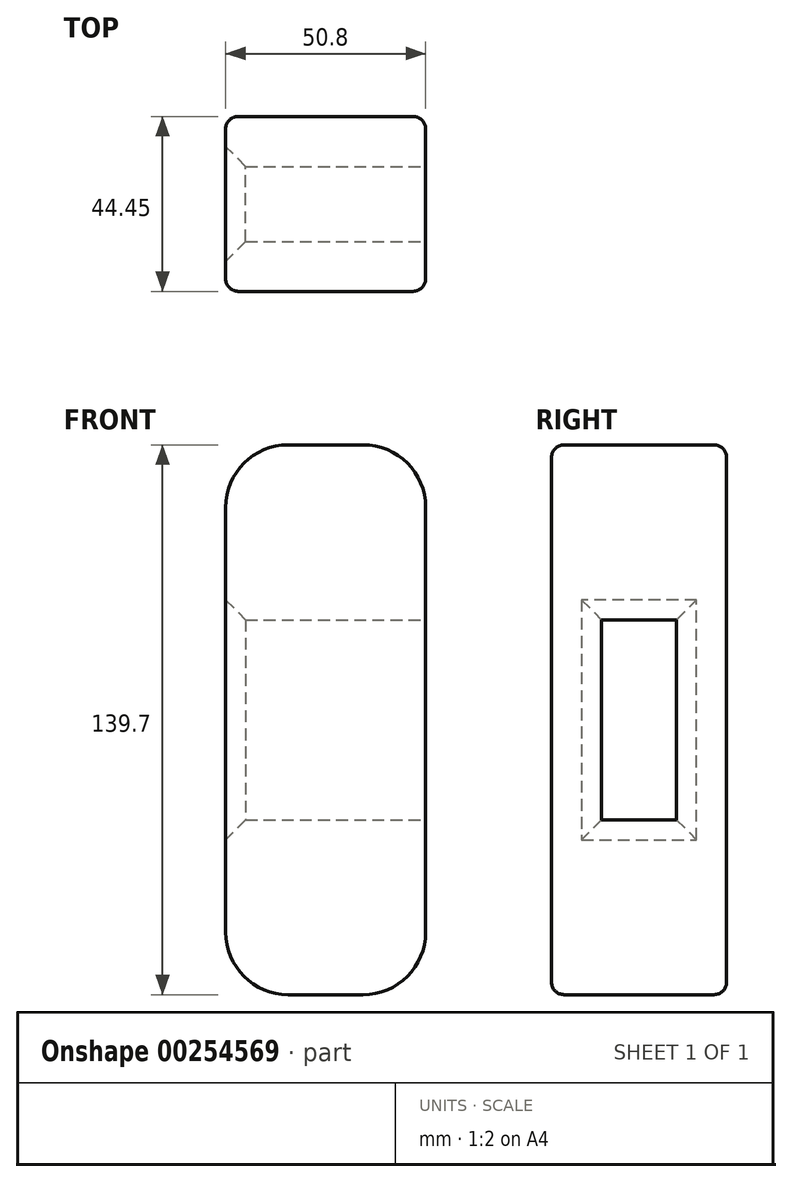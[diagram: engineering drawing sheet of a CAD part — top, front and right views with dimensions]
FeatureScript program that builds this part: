
annotation { "Feature Type Name" : "Feature", "Feature Type Description" : "" }
export const myFeature = defineFeature(function(context is Context, id is Id, definition is map)
    precondition{}
    {
        {
            var Q0;
            Q0=qCreatedBy(makeId("Front.planeOp"),FACE);
            var sketch = newSketch(context, id + "F0", { "sketchPlane" : qUnion([Q0])});
            skLineSegment(sketch, "E0.bottom", {"start": v(9.52, 69.85) * mm, "end": v(-9.53, 69.85) * mm});
            skLineSegment(sketch, "E0.top", {"start": v(9.52, -69.85) * mm, "end": v(-9.53, -69.85) * mm});
            skLineSegment(sketch, "E0.left", {"start": v(25.4, 53.98) * mm, "end": v(25.4, -53.97) * mm});
            skLineSegment(sketch, "E0.right", {"start": v(-25.4, 53.98) * mm, "end": v(-25.4, -53.97) * mm});
            skPoint(sketch, "E0.middle", {"position": v(0, 0) * mm});
            skPoint(sketch, "E1.visualSharp", {"position": v(-25.4, 69.85) * mm});
            skArc(sketch, "E1.filletArc", {"start": v(-9.53, 69.85) * mm, "mid": v(-20.75, 65.2) * mm, "end": v(-25.4, 53.98) * mm});
            skPoint(sketch, "E2.visualSharp", {"position": v(25.4, 69.85) * mm});
            skArc(sketch, "E2.filletArc", {"start": v(25.4, 53.98) * mm, "mid": v(20.75, 65.2) * mm, "end": v(9.52, 69.85) * mm});
            skPoint(sketch, "E3.visualSharp", {"position": v(25.4, -69.85) * mm});
            skArc(sketch, "E3.filletArc", {"start": v(9.52, -69.85) * mm, "mid": v(20.75, -65.2) * mm, "end": v(25.4, -53.97) * mm});
            skPoint(sketch, "E4.visualSharp", {"position": v(-25.4, -69.85) * mm});
            skArc(sketch, "E4.filletArc", {"start": v(-25.4, -53.97) * mm, "mid": v(-20.75, -65.2) * mm, "end": v(-9.53, -69.85) * mm});
            skSolve(sketch);
        }
        {
            var Q0;
            Q0 = qSketchRegion(id + "F0", true);
            extrude(context, id + "F1", {"entities" : qUnion([Q0]), "depth" : 44.45 * mm});
        }
        {
            var Q0;
            Q0=makeQuery(id+"F1.opExtrude","CAP_FACE",FACE,{"disambiguationData":[OSD([sQuery(id+"F0.wireOp",EDGE,"E0.bottom"),sQuery(id+"F0.wireOp",EDGE,"E0.top"),sQuery(id+"F0.wireOp",EDGE,"E0.left"),sQuery(id+"F0.wireOp",EDGE,"E0.right"),sQuery(id+"F0.wireOp",EDGE,"E1.filletArc"),sQuery(id+"F0.wireOp",EDGE,"E2.filletArc"),sQuery(id+"F0.wireOp",EDGE,"E3.filletArc"),sQuery(id+"F0.wireOp",EDGE,"E4.filletArc")])],"isStart":false});
            var Q1;
            Q1=makeQuery(id+"F1.opExtrude","CAP_FACE",FACE,{"disambiguationData":[OSD([sQuery(id+"F0.wireOp",EDGE,"E0.bottom"),sQuery(id+"F0.wireOp",EDGE,"E0.top"),sQuery(id+"F0.wireOp",EDGE,"E0.left"),sQuery(id+"F0.wireOp",EDGE,"E0.right"),sQuery(id+"F0.wireOp",EDGE,"E1.filletArc"),sQuery(id+"F0.wireOp",EDGE,"E2.filletArc"),sQuery(id+"F0.wireOp",EDGE,"E3.filletArc"),sQuery(id+"F0.wireOp",EDGE,"E4.filletArc")])],"isStart":true});
            fillet(context, id + "F2", {"entities" : qUnion([Q0, Q1]), "radius" : 3.17 * mm, "tangentPropagation" : true, "allowEdgeOverflow" : false});
        }
        {
            var Q0;
            Q0=makeQuery(id+"F1.opExtrude","SWEPT_FACE",FACE,{"disambiguationData":[OSD([sQuery(id+"F0.wireOp",EDGE,"E0.left")])]});
            var sketch = newSketch(context, id + "F3", { "sketchPlane" : qUnion([Q0])});
            skLineSegment(sketch, "E5", {"start": v(-41.28, 0) * mm, "end": v(-22.23, 0) * mm});
            skPoint(sketch, "E5.endSnap0", {"position": v(-3.18, 0) * mm});
            skLineSegment(sketch, "E6.bottom", {"start": v(-12.7, 25.4) * mm, "end": v(-31.75, 25.4) * mm});
            skLineSegment(sketch, "E6.top", {"start": v(-12.7, -25.4) * mm, "end": v(-31.75, -25.4) * mm});
            skLineSegment(sketch, "E6.left", {"start": v(-12.7, 25.4) * mm, "end": v(-12.7, -25.4) * mm});
            skLineSegment(sketch, "E6.right", {"start": v(-31.75, 25.4) * mm, "end": v(-31.75, -25.4) * mm});
            skPoint(sketch, "E6.middle", {"position": v(-22.23, 0) * mm});
            skSolve(sketch);
        }
        {
            var Q0;
            {var subQ1=sQuery(id+"F3.wireOp",EDGE,"E6.bottom");Q0=makeQuery(id+"F3.imprint","IMPRINT",FACE,{"disambiguationData":[TD([[makeQuery(id+"F3.imprint","IMPRINT",EDGE,{"derivedFrom":subQ1}),1.0]])]});}
            extrude(context, id + "F4", {"entities" : qUnion([Q0]), "operationType" : NewBodyOperationType.REMOVE, "endBound" : BoundingType.THROUGH_ALL, "oppositeDirection" : true, "depth" : 25.4 * mm});
        }
        {
            var Q0;
            Q0=makeQuery(id+"F4.boolean.opBoolean","INTERSECT",EDGE,{"derivedFrom":[makeQuery(id+"F1.opExtrude","SWEPT_FACE",FACE,{"disambiguationData":[OSD([sQuery(id+"F0.wireOp",EDGE,"E0.right")])]}),makeQuery(id+"F4.opExtrude","SWEPT_FACE",FACE,{"disambiguationData":[OSD([sQuery(id+"F3.wireOp",EDGE,"E6.top")])]})]});
            var Q1;
            Q1=makeQuery(id+"F4.boolean.opBoolean","INTERSECT",EDGE,{"derivedFrom":[makeQuery(id+"F1.opExtrude","SWEPT_FACE",FACE,{"disambiguationData":[OSD([sQuery(id+"F0.wireOp",EDGE,"E0.right")])]}),makeQuery(id+"F4.opExtrude","SWEPT_FACE",FACE,{"disambiguationData":[OSD([sQuery(id+"F3.wireOp",EDGE,"E6.right")])]})]});
            var Q2;
            Q2=makeQuery(id+"F4.boolean.opBoolean","INTERSECT",EDGE,{"derivedFrom":[makeQuery(id+"F1.opExtrude","SWEPT_FACE",FACE,{"disambiguationData":[OSD([sQuery(id+"F0.wireOp",EDGE,"E0.right")])]}),makeQuery(id+"F4.opExtrude","SWEPT_FACE",FACE,{"disambiguationData":[OSD([sQuery(id+"F3.wireOp",EDGE,"E6.left")])]})]});
            var Q3;
            Q3=makeQuery(id+"F4.boolean.opBoolean","INTERSECT",EDGE,{"derivedFrom":[makeQuery(id+"F1.opExtrude","SWEPT_FACE",FACE,{"disambiguationData":[OSD([sQuery(id+"F0.wireOp",EDGE,"E0.right")])]}),makeQuery(id+"F4.opExtrude","SWEPT_FACE",FACE,{"disambiguationData":[OSD([sQuery(id+"F3.wireOp",EDGE,"E6.bottom")])]})]});
            var Q4;
            Q4=makeQuery(id+"F4.boolean.opBoolean","COPY",EDGE,{"derivedFrom":makeQuery(id+"F4.opExtrude","CAP_EDGE",EDGE,{"disambiguationData":[OSD([sQuery(id+"F3.wireOp",EDGE,"E6.top")])],"isStart":true})});
            var Q5;
            Q5=makeQuery(id+"F4.boolean.opBoolean","COPY",EDGE,{"derivedFrom":makeQuery(id+"F4.opExtrude","CAP_EDGE",EDGE,{"disambiguationData":[OSD([sQuery(id+"F3.wireOp",EDGE,"E6.right")])],"isStart":true})});
            var Q6;
            Q6=makeQuery(id+"F4.boolean.opBoolean","COPY",EDGE,{"derivedFrom":makeQuery(id+"F4.opExtrude","CAP_EDGE",EDGE,{"disambiguationData":[OSD([sQuery(id+"F3.wireOp",EDGE,"E6.left")])],"isStart":true})});
            var Q7;
            Q7=makeQuery(id+"F4.boolean.opBoolean","COPY",EDGE,{"derivedFrom":makeQuery(id+"F4.opExtrude","CAP_EDGE",EDGE,{"disambiguationData":[OSD([sQuery(id+"F3.wireOp",EDGE,"E6.bottom")])],"isStart":true})});
            chamfer(context, id + "F5", {"entities" : qUnion([Q0, Q1, Q2, Q3, Q4, Q5, Q6, Q7]), "width" : 5.08 * mm, "tangentPropagation" : true});
        }
    });
